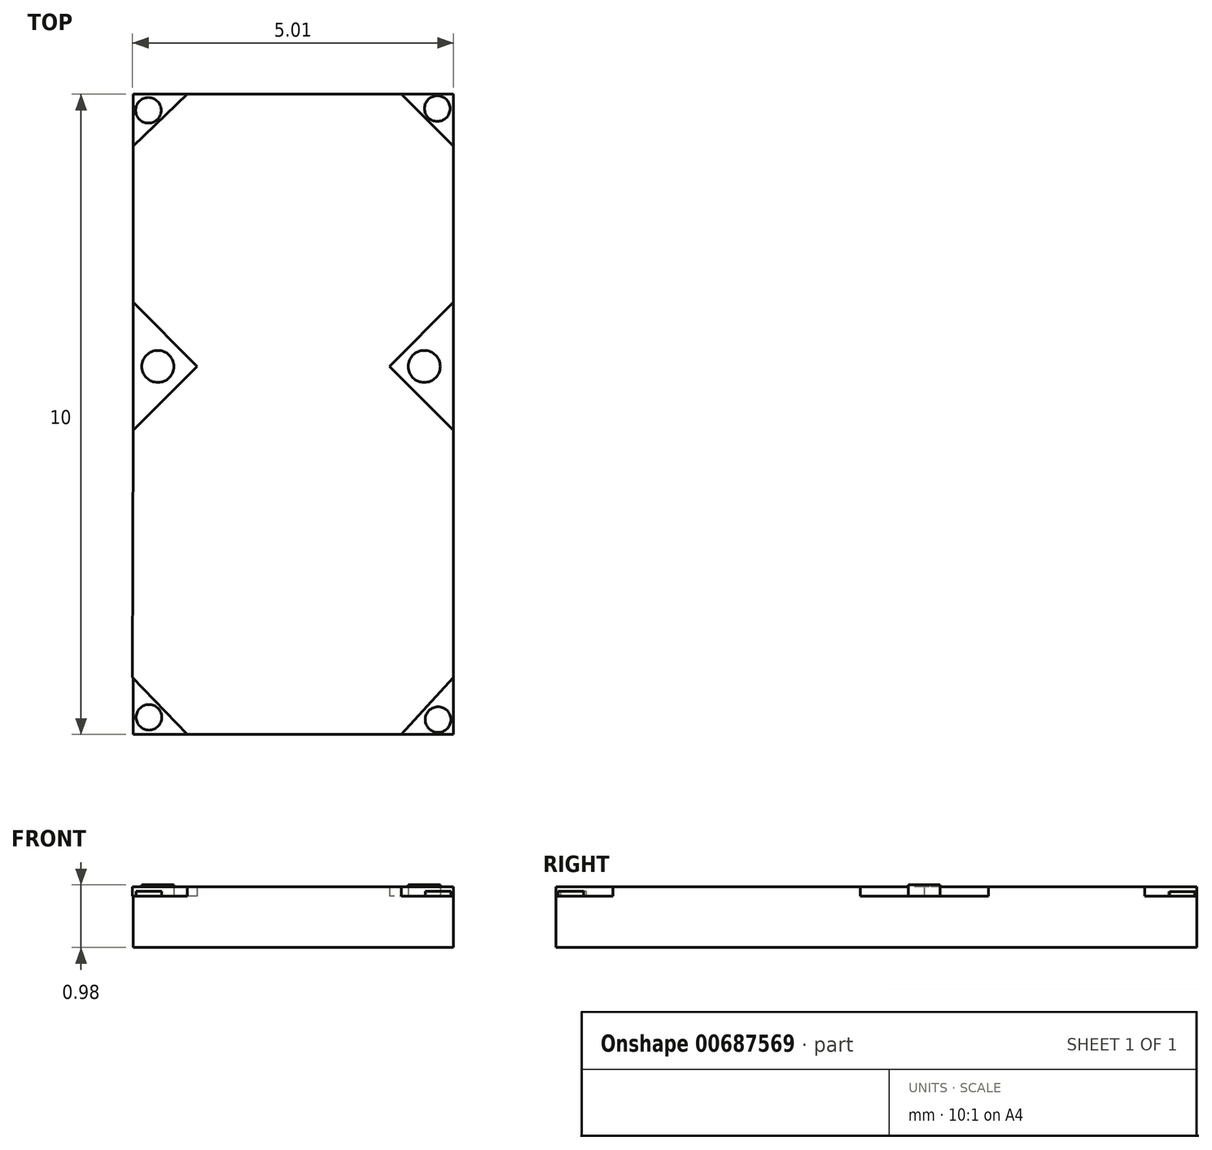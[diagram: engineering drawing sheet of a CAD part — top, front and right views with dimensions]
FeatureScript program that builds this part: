
annotation { "Feature Type Name" : "Feature", "Feature Type Description" : "" }
export const myFeature = defineFeature(function(context is Context, id is Id, definition is map)
    precondition{}
    {
        {
            var Q0;
            Q0=qCreatedBy(makeId("Top.planeOp"),FACE);
            var sketch = newSketch(context, id + "F0", { "sketchPlane" : qUnion([Q0])});
            skLineSegment(sketch, "E0.bottom", {"start": v(0, 0) * mm, "end": v(-5, 0) * mm});
            skLineSegment(sketch, "E0.top", {"start": v(0, 10) * mm, "end": v(-5, 10) * mm});
            skLineSegment(sketch, "E0.left", {"start": v(0, 0) * mm, "end": v(0, 10) * mm});
            skLineSegment(sketch, "E0.right", {"start": v(-5, 0) * mm, "end": v(-5, 10) * mm});
            skSolve(sketch);
        }
        {
            var Q0;
            Q0=makeQuery(id+"F0.imprint","IMPRINT",FACE,{"disambiguationData":[TD([[makeQuery(id+"F0.imprint","IMPRINT",EDGE,{"derivedFrom":sQuery(id+"F0.wireOp",EDGE,"E0.bottom")}),-1.0]])]});
            extrude(context, id + "F1", {"entities" : qUnion([Q0]), "depth" : 0.8 * mm, "offsetDistance" : 25 * mm});
        }
        {
            var Q0;
            Q0=makeQuery(id+"F1.opExtrude","CAP_FACE",FACE,{"disambiguationData":[OSD([sQuery(id+"F0.wireOp",EDGE,"E0.bottom"),sQuery(id+"F0.wireOp",EDGE,"E0.top"),sQuery(id+"F0.wireOp",EDGE,"E0.left"),sQuery(id+"F0.wireOp",EDGE,"E0.right")])],"isStart":false});
            var sketch = newSketch(context, id + "F2", { "sketchPlane" : qUnion([Q0])});
            skLineSegment(sketch, "E1", {"start": v(-5, 9.19) * mm, "end": v(-4.15, 10) * mm});
            skLineSegment(sketch, "E2", {"start": v(-4.15, 10) * mm, "end": v(-0.81, 10) * mm});
            skLineSegment(sketch, "E3", {"start": v(-0.81, 10) * mm, "end": v(0, 9.19) * mm});
            skLineSegment(sketch, "E4", {"start": v(0, 0.9) * mm, "end": v(-0.81, 0) * mm});
            skLineSegment(sketch, "E5", {"start": v(-0.81, 0) * mm, "end": v(-4.15, 0) * mm});
            skLineSegment(sketch, "E6", {"start": v(-4.15, 0) * mm, "end": v(-5, 0.9) * mm});
            skPoint(sketch, "E7.start.orphan", {"position": v(-4.38, 5.3) * mm});
            skPoint(sketch, "E8.end.orphan", {"position": v(-0.7, 5.3) * mm});
            skPoint(sketch, "E9.orphan", {"position": v(-5, 5.25) * mm});
            skPoint(sketch, "E10.start.orphan", {"position": v(0, 4.25) * mm});
            skPoint(sketch, "E11.end.orphan", {"position": v(-5, 6.24) * mm});
            skPoint(sketch, "E12.start.orphan", {"position": v(-5, 4.25) * mm});
            skPoint(sketch, "E13.start.orphan", {"position": v(0, 6.24) * mm});
            skLineSegment(sketch, "E14", {"start": v(-5, 9.19) * mm, "end": v(-5, 6.75) * mm});
            skLineSegment(sketch, "E15", {"start": v(0, 6.75) * mm, "end": v(0, 9.19) * mm});
            skLineSegment(sketch, "E16", {"start": v(0, 4.75) * mm, "end": v(0, 0.9) * mm});
            skLineSegment(sketch, "E17", {"start": v(0, 9.19) * mm, "end": v(0, 6.75) * mm});
            skLineSegment(sketch, "E18", {"start": v(-5, 6.75) * mm, "end": v(-4, 5.75) * mm});
            skLineSegment(sketch, "E19", {"start": v(-4, 5.75) * mm, "end": v(-5, 4.75) * mm});
            skLineSegment(sketch, "E20", {"start": v(0, 6.75) * mm, "end": v(-1, 5.75) * mm});
            skLineSegment(sketch, "E21", {"start": v(-1, 5.75) * mm, "end": v(0, 4.75) * mm});
            skPoint(sketch, "E22.end.orphan", {"position": v(-4, 6.75) * mm});
            skPoint(sketch, "E23.end.orphan", {"position": v(-4, 4.75) * mm});
            skPoint(sketch, "E24.end.orphan", {"position": v(-5, 5.75) * mm});
            skPoint(sketch, "E25.end.orphan", {"position": v(0, 5.75) * mm});
            skPoint(sketch, "E26.end.orphan", {"position": v(-1, 4.75) * mm});
            skPoint(sketch, "E27.start.orphan", {"position": v(-1, 6.75) * mm});
            skLineSegment(sketch, "E28", {"start": v(-5, 4.75) * mm, "end": v(-5, 0.9) * mm});
            skSolve(sketch);
        }
        {
            var Q0;
            Q0 = qSketchRegion(id + "F2", true);
            extrude(context, id + "F3", {"entities" : qUnion([Q0]), "operationType" : NewBodyOperationType.ADD, "depth" : 0.15 * mm, "offsetDistance" : 25 * mm});
        }
        {
            var Q0;
            {var subQ0=sQuery(id+"F0.wireOp",EDGE,"E0.right");Q0=makeQuery(id+"F3.boolean.opBoolean","SPLIT",FACE,{"disambiguationData":[TD([makeQuery(id+"F3.opExtrude","SWEPT_FACE",FACE,{"disambiguationData":[OSD([sQuery(id+"F2.wireOp",EDGE,"E18")])]})])],"derivedFrom":makeQuery(id+"F1.opExtrude","CAP_FACE",FACE,{"disambiguationData":[OSD([sQuery(id+"F0.wireOp",EDGE,"E0.bottom"),sQuery(id+"F0.wireOp",EDGE,"E0.top"),sQuery(id+"F0.wireOp",EDGE,"E0.left"),subQ0])],"isStart":false})});}
            var sketch = newSketch(context, id + "F4", { "sketchPlane" : qUnion([Q0])});
            skCircle(sketch, "E29", {"center": v(-4.61, 5.75) * mm, "radius": 0.25 * mm});
            skCircle(sketch, "E30", {"center": v(-0.46, 5.75) * mm, "radius": 0.25 * mm});
            skSolve(sketch);
        }
        {
            var Q0;
            Q0 = qSketchRegion(id + "F4", true);
            extrude(context, id + "F5", {"entities" : qUnion([Q0]), "operationType" : NewBodyOperationType.ADD, "depth" : 0.18 * mm, "offsetDistance" : 25 * mm});
        }
        {
            var Q0;
            {var subQ0=sQuery(id+"F0.wireOp",EDGE,"E0.right");var subQ1=sQuery(id+"F0.wireOp",EDGE,"E0.bottom");Q0=makeQuery(id+"F3.boolean.opBoolean","SPLIT",FACE,{"disambiguationData":[TD([makeQuery(id+"F3.opExtrude","SWEPT_FACE",FACE,{"disambiguationData":[OSD([sQuery(id+"F2.wireOp",EDGE,"E6")])]})])],"derivedFrom":makeQuery(id+"F1.opExtrude","CAP_FACE",FACE,{"disambiguationData":[OSD([subQ1,sQuery(id+"F0.wireOp",EDGE,"E0.top"),sQuery(id+"F0.wireOp",EDGE,"E0.left"),subQ0])],"isStart":false})});}
            var sketch = newSketch(context, id + "F6", { "sketchPlane" : qUnion([Q0])});
            skCircle(sketch, "E31", {"center": v(-4.75, 0.27) * mm, "radius": 0.2 * mm});
            skCircle(sketch, "E32", {"center": v(-0.24, 0.23) * mm, "radius": 0.2 * mm});
            skSolve(sketch);
        }
        {
            var Q0;
            Q0 = qSketchRegion(id + "F6", true);
            extrude(context, id + "F7", {"entities" : qUnion([Q0]), "operationType" : NewBodyOperationType.ADD, "depth" : 0.08 * mm, "offsetDistance" : 25 * mm});
        }
        {
            var Q0;
            {var subQ0=sQuery(id+"F0.wireOp",EDGE,"E0.right");var subQ1=sQuery(id+"F0.wireOp",EDGE,"E0.top");Q0=makeQuery(id+"F3.boolean.opBoolean","SPLIT",FACE,{"disambiguationData":[TD([makeQuery(id+"F3.opExtrude","SWEPT_FACE",FACE,{"disambiguationData":[OSD([sQuery(id+"F2.wireOp",EDGE,"E1")])]})])],"derivedFrom":makeQuery(id+"F1.opExtrude","CAP_FACE",FACE,{"disambiguationData":[OSD([sQuery(id+"F0.wireOp",EDGE,"E0.bottom"),subQ1,sQuery(id+"F0.wireOp",EDGE,"E0.left"),subQ0])],"isStart":false})});}
            var sketch = newSketch(context, id + "F8", { "sketchPlane" : qUnion([Q0])});
            skCircle(sketch, "E33", {"center": v(-4.76, 9.75) * mm, "radius": 0.2 * mm});
            skCircle(sketch, "E34", {"center": v(-0.25, 9.77) * mm, "radius": 0.2 * mm});
            skSolve(sketch);
        }
        {
            var Q0;
            Q0 = qSketchRegion(id + "F8", true);
            extrude(context, id + "F9", {"entities" : qUnion([Q0]), "operationType" : NewBodyOperationType.ADD, "depth" : 0.07 * mm, "offsetDistance" : 25 * mm});
        }
    });
